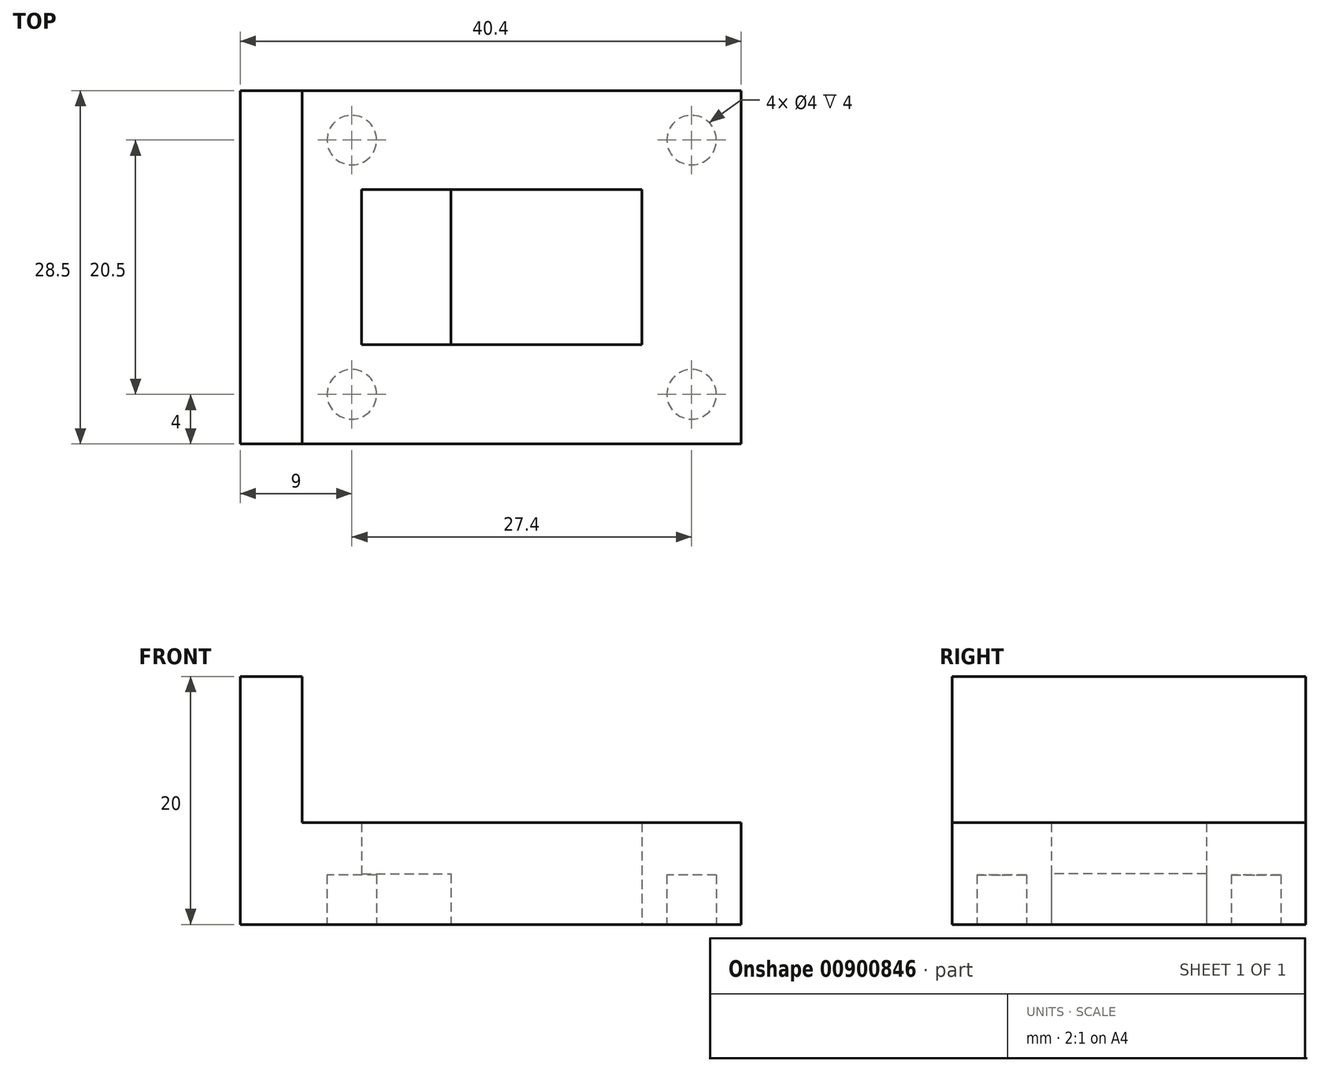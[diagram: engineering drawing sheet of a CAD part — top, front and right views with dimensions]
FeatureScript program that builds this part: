
annotation { "Feature Type Name" : "Feature", "Feature Type Description" : "" }
export const myFeature = defineFeature(function(context is Context, id is Id, definition is map)
    precondition{}
    {
        {
            var Q0;
            Q0=qCreatedBy(makeId("Top.planeOp"),FACE);
            var sketch = newSketch(context, id + "F0", { "sketchPlane" : qUnion([Q0])});
            skLineSegment(sketch, "E0.bottom", {"start": v(-14.65, 13.55) * mm, "end": v(20.75, 13.55) * mm});
            skLineSegment(sketch, "E0.top", {"start": v(-14.65, -14.95) * mm, "end": v(20.75, -14.95) * mm});
            skLineSegment(sketch, "E0.left", {"start": v(-14.65, 13.55) * mm, "end": v(-14.65, -14.95) * mm});
            skLineSegment(sketch, "E0.right", {"start": v(20.75, 13.55) * mm, "end": v(20.75, -14.95) * mm});
            skLineSegment(sketch, "E1.bottom", {"start": v(-9.85, 5.55) * mm, "end": v(12.75, 5.55) * mm});
            skLineSegment(sketch, "E1.top", {"start": v(-9.85, -6.95) * mm, "end": v(12.75, -6.95) * mm});
            skLineSegment(sketch, "E1.left", {"start": v(-9.85, 5.55) * mm, "end": v(-9.85, -6.95) * mm});
            skLineSegment(sketch, "E1.right", {"start": v(12.75, 5.55) * mm, "end": v(12.75, -6.95) * mm});
            skLineSegment(sketch, "E2.bottom", {"start": v(-14.65, 13.55) * mm, "end": v(-19.65, 13.55) * mm});
            skLineSegment(sketch, "E2.top", {"start": v(-14.65, -14.95) * mm, "end": v(-19.65, -14.95) * mm});
            skLineSegment(sketch, "E2.right", {"start": v(-19.65, 13.55) * mm, "end": v(-19.65, -14.95) * mm});
            skLineSegment(sketch, "E3.bottom", {"start": v(-9.85, 5.55) * mm, "end": v(-2.65, 5.55) * mm});
            skLineSegment(sketch, "E3.top", {"start": v(-9.85, -6.95) * mm, "end": v(-2.65, -6.95) * mm});
            skLineSegment(sketch, "E3.right", {"start": v(-2.65, 5.55) * mm, "end": v(-2.65, -6.95) * mm});
            skCircle(sketch, "E4", {"center": v(16.75, 9.55) * mm, "radius": 2 * mm});
            skCircle(sketch, "E5", {"center": v(16.75, -10.95) * mm, "radius": 2 * mm});
            skCircle(sketch, "E6", {"center": v(-10.65, -10.95) * mm, "radius": 2 * mm});
            skCircle(sketch, "E7", {"center": v(-10.65, 9.55) * mm, "radius": 2 * mm});
            skSolve(sketch);
        }
        {
            var Q0;
            Q0=makeQuery(id+"F0.imprint","IMPRINT",FACE,{"disambiguationData":[TD([[makeQuery(id+"F0.imprint","IMPRINT",EDGE,{"derivedFrom":sQuery(id+"F0.wireOp",EDGE,"E0.bottom")}),-1.0]])]});
            var Q1;
            Q1=makeQuery(id+"F0.imprint","IMPRINT",FACE,{"disambiguationData":[TD([[makeQuery(id+"F0.imprint","IMPRINT",EDGE,{"derivedFrom":sQuery(id+"F0.wireOp",EDGE,"E7")}),1.0]])]});
            var Q2;
            Q2=makeQuery(id+"F0.imprint","IMPRINT",FACE,{"disambiguationData":[TD([[makeQuery(id+"F0.imprint","IMPRINT",EDGE,{"derivedFrom":sQuery(id+"F0.wireOp",EDGE,"E4")}),1.0]])]});
            var Q3;
            Q3=makeQuery(id+"F0.imprint","IMPRINT",FACE,{"disambiguationData":[TD([[makeQuery(id+"F0.imprint","IMPRINT",EDGE,{"derivedFrom":sQuery(id+"F0.wireOp",EDGE,"E5")}),1.0]])]});
            var Q4;
            Q4=makeQuery(id+"F0.imprint","IMPRINT",FACE,{"disambiguationData":[TD([[makeQuery(id+"F0.imprint","IMPRINT",EDGE,{"derivedFrom":sQuery(id+"F0.wireOp",EDGE,"E6")}),1.0]])]});
            extrude(context, id + "F1", {"entities" : qUnion([Q0, Q1, Q2, Q3, Q4]), "depth" : 8.2 * mm, "offsetDistance" : 25 * mm});
        }
        {
            var Q0;
            Q0=makeQuery(id+"F0.imprint","IMPRINT",FACE,{"disambiguationData":[TD([[makeQuery(id+"F0.imprint","IMPRINT",EDGE,{"derivedFrom":sQuery(id+"F0.wireOp",EDGE,"E0.left")}),-1.0]])]});
            extrude(context, id + "F2", {"entities" : qUnion([Q0]), "operationType" : NewBodyOperationType.ADD, "depth" : 20 * mm, "offsetDistance" : 25 * mm});
        }
        {
            var Q0;
            {var subQ2=sQuery(id+"F0.wireOp",EDGE,"E1.left");Q0=makeQuery(id+"F0.imprint","IMPRINT",FACE,{"disambiguationData":[TD([[makeQuery(id+"F0.imprint","IMPRINT",EDGE,{"derivedFrom":subQ2}),1.0]])]});}
            extrude(context, id + "F3", {"entities" : qUnion([Q0]), "operationType" : NewBodyOperationType.ADD, "depth" : 4.08 * mm, "offsetDistance" : 25 * mm});
        }
        {
            var Q0;
            Q0=makeQuery(id+"F0.imprint","IMPRINT",FACE,{"disambiguationData":[TD([[makeQuery(id+"F0.imprint","IMPRINT",EDGE,{"derivedFrom":sQuery(id+"F0.wireOp",EDGE,"E6")}),1.0]])]});
            var Q1;
            Q1=makeQuery(id+"F0.imprint","IMPRINT",FACE,{"disambiguationData":[TD([[makeQuery(id+"F0.imprint","IMPRINT",EDGE,{"derivedFrom":sQuery(id+"F0.wireOp",EDGE,"E5")}),1.0]])]});
            var Q2;
            Q2=makeQuery(id+"F0.imprint","IMPRINT",FACE,{"disambiguationData":[TD([[makeQuery(id+"F0.imprint","IMPRINT",EDGE,{"derivedFrom":sQuery(id+"F0.wireOp",EDGE,"E4")}),1.0]])]});
            var Q3;
            Q3=makeQuery(id+"F0.imprint","IMPRINT",FACE,{"disambiguationData":[TD([[makeQuery(id+"F0.imprint","IMPRINT",EDGE,{"derivedFrom":sQuery(id+"F0.wireOp",EDGE,"E7")}),1.0]])]});
            extrude(context, id + "F4", {"entities" : qUnion([Q0, Q1, Q2, Q3]), "operationType" : NewBodyOperationType.REMOVE, "depth" : 4 * mm, "offsetDistance" : 25 * mm});
        }
    });
